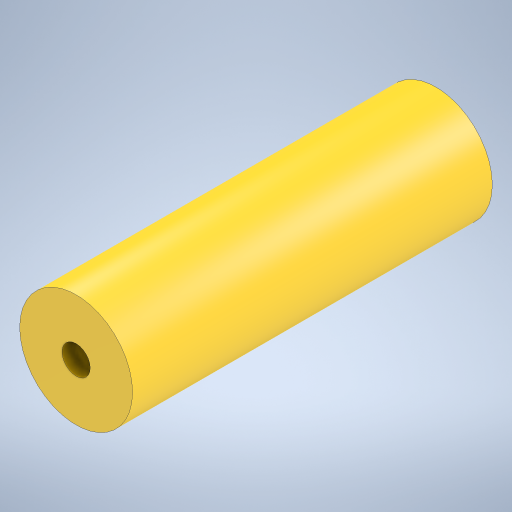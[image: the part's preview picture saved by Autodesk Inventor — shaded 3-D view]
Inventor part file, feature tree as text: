
AUTODESK INVENTOR PART (.ipt)
format: ipt  version: 2023 (Build 270158030, 158C)  size: 228,864 bytes
history: native  units: mm
features: extrude x1, sketch x1
ambient origin geometry x8: Origin, YZ Plane, XZ Plane, XY Plane, X Axis, Y Axis, Z Axis, Center Point
bodies: Solid1 (feature_tree)
feature tree (2):
  extrude  "Extrusion1"  Depth=20.0mm
  sketch  "Sketch1"  dims[d0=80.0mm d1=20.0mm d2=250.0mm d3=5.0mm d4=0.0mm d5=0.0mm]
